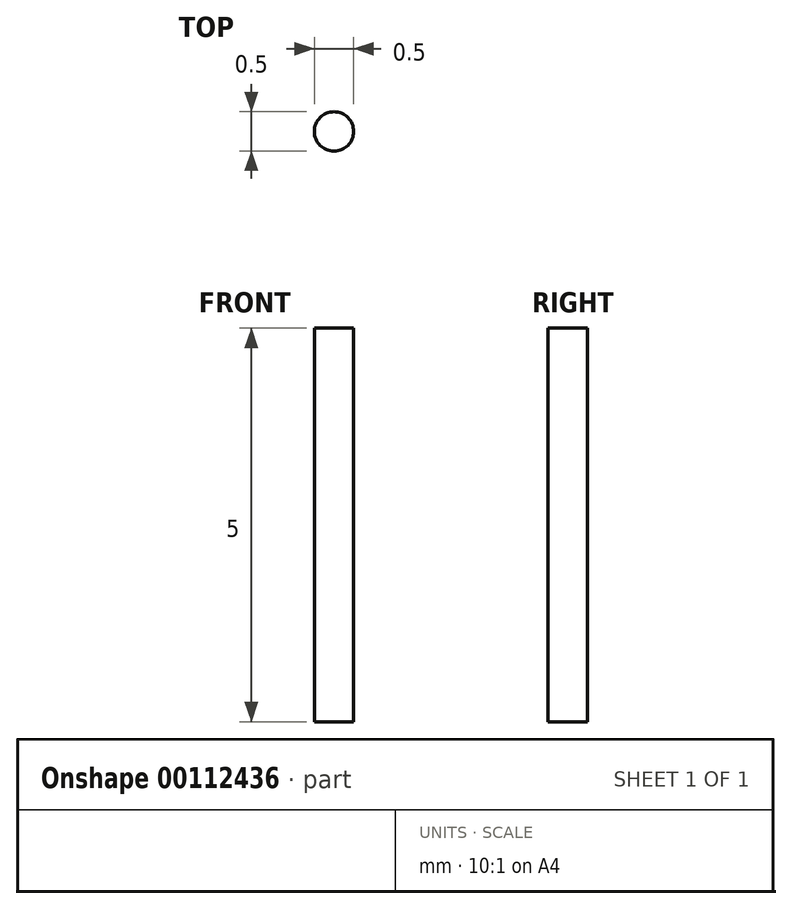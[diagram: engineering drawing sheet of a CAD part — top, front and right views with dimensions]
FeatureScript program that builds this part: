
annotation { "Feature Type Name" : "Feature", "Feature Type Description" : "" }
export const myFeature = defineFeature(function(context is Context, id is Id, definition is map)
    precondition{}
    {
        {
            var Q0;
            Q0=qCreatedBy(makeId("Top.planeOp"),FACE);
            var sketch = newSketch(context, id + "F0", { "sketchPlane" : qUnion([Q0])});
            skCircle(sketch, "E0", {"center": v(0, 0) * mm, "radius": 0.25 * mm});
            skSolve(sketch);
        }
        {
            var Q0;
            Q0 = qSketchRegion(id + "F0", true);
            extrude(context, id + "F1", {"entities" : qUnion([Q0]), "depth" : 5 * mm});
        }
    });
